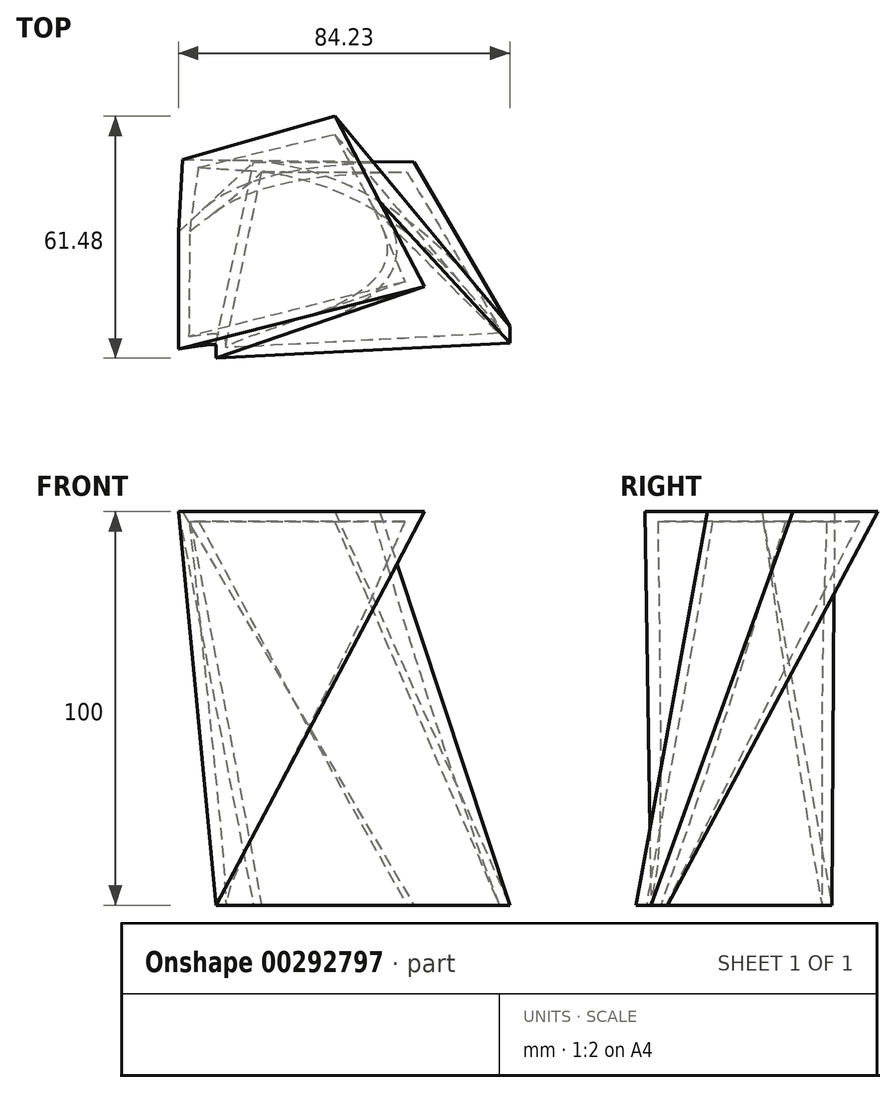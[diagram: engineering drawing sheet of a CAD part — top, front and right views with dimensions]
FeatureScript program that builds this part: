
annotation { "Feature Type Name" : "Feature", "Feature Type Description" : "" }
export const myFeature = defineFeature(function(context is Context, id is Id, definition is map)
    precondition{}
    {
        {
            var Q0;
            Q0=qCreatedBy(makeId("Top.planeOp"),FACE);
            var sketch = newSketch(context, id + "F0", { "sketchPlane" : qUnion([Q0])});
            skLineSegment(sketch, "E0", {"start": v(-16.95, -35.3) * mm, "end": v(-16.95, -31.48) * mm});
            skLineSegment(sketch, "E1", {"start": v(-16.95, -31.48) * mm, "end": v(-7.43, 14.49) * mm});
            skLineSegment(sketch, "E2", {"start": v(-7.43, 14.49) * mm, "end": v(33.37, 14.49) * mm});
            skLineSegment(sketch, "E3", {"start": v(33.37, 14.49) * mm, "end": v(57.7, -27.25) * mm});
            skLineSegment(sketch, "E4", {"start": v(57.7, -27.25) * mm, "end": v(57.7, -31.48) * mm});
            skLineSegment(sketch, "E5", {"start": v(57.7, -31.48) * mm, "end": v(-16.95, -35.3) * mm});
            skSolve(sketch);
        }
        {
            var Q0;
            Q0=qCreatedBy(makeId("Top.planeOp"),FACE);
            cPlane(context, id + "F1", {"entities" : qUnion([Q0]), "cplaneType" : CPlaneType.OFFSET, "offset" : 100 * mm, "width" : 150 * mm, "height" : 150 * mm});
        }
        {
            var Q0;
            Q0=qCreatedBy(id+"F1.planeOp",FACE);
            var sketch = newSketch(context, id + "F2", { "sketchPlane" : qUnion([Q0])});
            skLineSegment(sketch, "E6", {"start": v(-26.53, -3.3) * mm, "end": v(-26.53, -33) * mm});
            skLineSegment(sketch, "E7", {"start": v(-26.53, -33) * mm, "end": v(36.05, -17.08) * mm});
            skLineSegment(sketch, "E8", {"start": v(36.05, -17.08) * mm, "end": v(13.2, 26.18) * mm});
            skLineSegment(sketch, "E9", {"start": v(13.2, 26.18) * mm, "end": v(-25.48, 15.16) * mm});
            skLineSegment(sketch, "E10", {"start": v(-25.48, 15.16) * mm, "end": v(-26.53, -3.3) * mm});
            skSolve(sketch);
        }
        {
            var Q0;
            Q0=makeQuery(id+"F2.imprint","IMPRINT",FACE,{"disambiguationData":[TD([[makeQuery(id+"F2.imprint","IMPRINT",EDGE,{"derivedFrom":sQuery(id+"F2.wireOp",EDGE,"E6")}),1.0]])]});
            var Q1;
            Q1=makeQuery(id+"F0.imprint","IMPRINT",FACE,{"disambiguationData":[TD([[makeQuery(id+"F0.imprint","IMPRINT",EDGE,{"derivedFrom":sQuery(id+"F0.wireOp",EDGE,"E0")}),-1.0]])]});
            loft(context, id + "F3", {"sheetProfilesArray" : [{ "sheetProfileEntities" : qUnion([Q0]) }, { "sheetProfileEntities" : qUnion([Q1]) }]});
        }
        {
            var Q0;
            Q0=makeQuery(id+"F3.opLoft","CAP_FACE",FACE,{"disambiguationData":[OSD([makeQuery(id+"F0.imprint","IMPRINT",FACE,{"disambiguationData":[TD([[makeQuery(id+"F0.imprint","IMPRINT",EDGE,{"derivedFrom":sQuery(id+"F0.wireOp",EDGE,"E0")}),-1.0]])]})])],"isStart":true});
            shell(context, id + "F4", {"entities" : qUnion([Q0]), "thickness" : 2.5 * mm});
        }
    });
